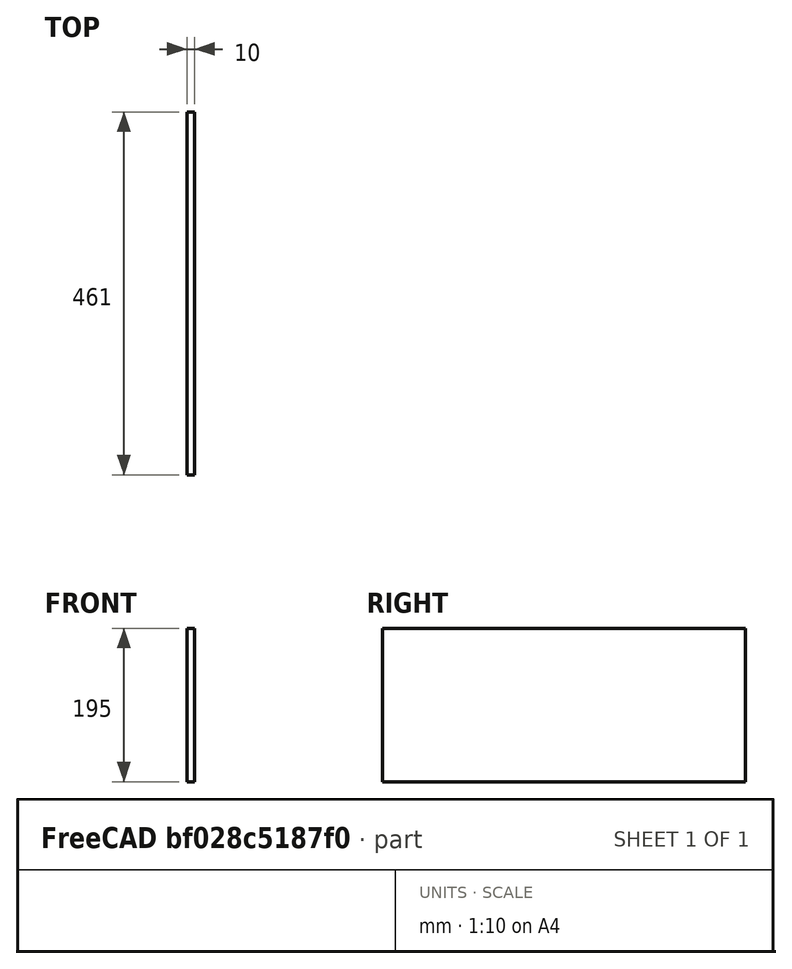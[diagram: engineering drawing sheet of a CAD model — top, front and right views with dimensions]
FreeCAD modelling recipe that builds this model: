
FCSTD DOCUMENT  (FreeCAD 0.18R16131 (Git))
Label: 500_Front_Horizontal
License: All rights reserved
LicenseURL: http://en.wikipedia.org/wiki/All_rights_reserved
objects: Sketcher::SketchObject×1, Spreadsheet::Sheet×1, PartDesign::Pad×1, PartDesign::Body×1
note: 4 computed .brp shape members not serialized (recipe doc carries the construction recipe); baked Part::Feature solids carry a one-line shape summary decoded from their .brp

FEATURE [Sketcher::SketchObject] Sketch
  MapMode = 4
  Placement = pos=(0,0,0) rot=(0.57735,0.57735,0.57735;2.0944rad)
  Support = -> [XY_Plane]
  expr: Constraints[6] = Spreadsheet.nY
  expr: Constraints[5] = Spreadsheet.nZ
  sketch-geometry (5):
    g0: LineSegment StartX=0 StartY=1e-16 StartZ=0 EndX=0 EndY=195 EndZ=0
    g1: LineSegment StartX=461 StartY=1e-16 StartZ=0 EndX=461 EndY=195 EndZ=0
    g2: LineSegment StartX=461 StartY=195 StartZ=0 EndX=0 EndY=195 EndZ=0
    g3: LineSegment StartX=230.5 StartY=1e-16 StartZ=0 EndX=0 EndY=1e-16 EndZ=0
    g4: LineSegment StartX=461 StartY=1e-16 StartZ=0 EndX=230.5 EndY=1e-16 EndZ=0
  constraints (14):
    c: Vertical(g0)
    c: Vertical(g1)
    c: Coincident(g2,g1)
    c: Coincident(g2,g0)
    c: Horizontal(g2)
    c: DistanceY(g1,g1) = 195
    c: DistanceX(g2,g2) = 461
    c: Coincident(g3,g0)
    c: Coincident(g4,g1)
    c: Horizontal(g4)
    c: Equal(g3,g4)
    c: Coincident(g4,g3)
    c: Horizontal(g3)
    c: Coincident(g0,g-1)
FEATURE [Spreadsheet::Sheet] Spreadsheet  label="xls"
  cells = B7=KEYBOARD FRONT; B8=Width; C8=nY; D8(nY)==480 - 19; B9=Height; C9=nZ; D9(nZ)=195; E9=F(T); B10=Thickness; C10=nT; D10(nT)=10
FEATURE [PartDesign::Pad] Pad
  Length = 10
  Length2 = 100
  Profile = -> Sketch
  Reversed = true
  Type = 0
  expr: Length = Spreadsheet.nT
FEATURE [PartDesign::Body] Body
  Group = -> [Sketch,Pad]
  Origin = -> Origin
  Tip = -> Pad
